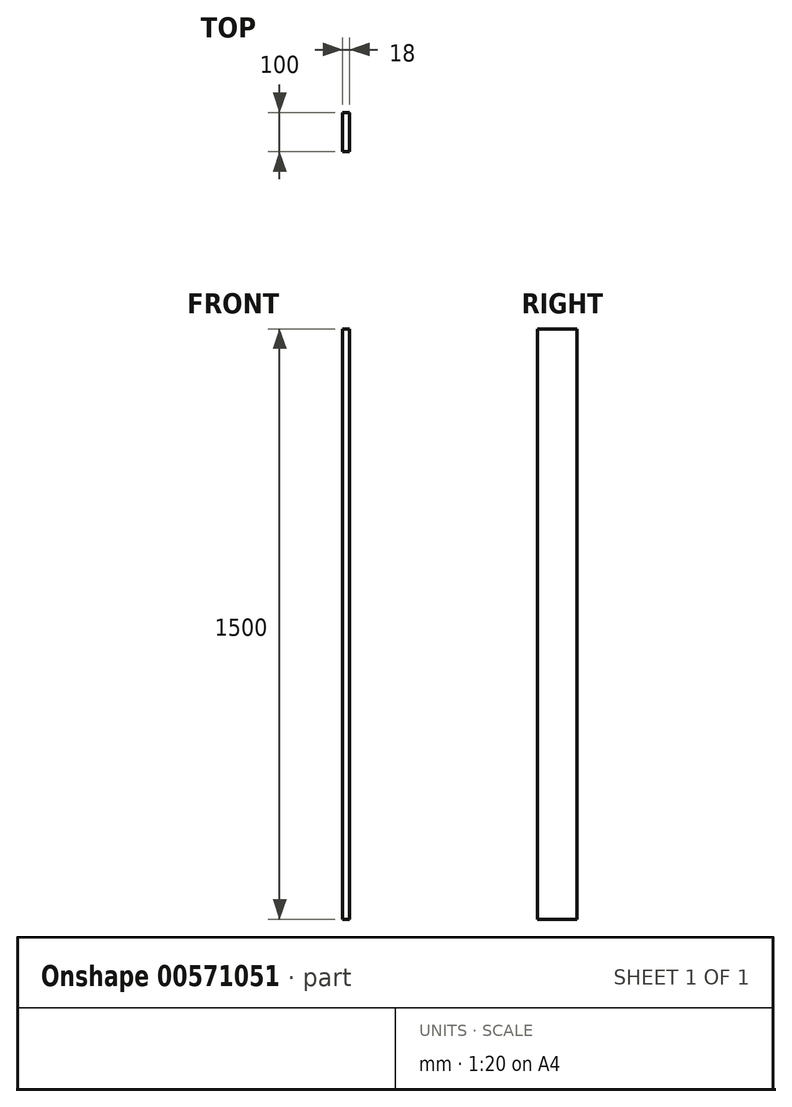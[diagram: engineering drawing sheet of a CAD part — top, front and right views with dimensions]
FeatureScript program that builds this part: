
annotation { "Feature Type Name" : "Feature", "Feature Type Description" : "" }
export const myFeature = defineFeature(function(context is Context, id is Id, definition is map)
    precondition{}
    {
        {
            var Q0;
            Q0=qCreatedBy(makeId("Right.planeOp"),FACE);
            var sketch = newSketch(context, id + "F0", { "sketchPlane" : qUnion([Q0])});
            skLineSegment(sketch, "E0.bottom", {"start": v(50, -750) * mm, "end": v(-50, -750) * mm});
            skLineSegment(sketch, "E0.top", {"start": v(50, 750) * mm, "end": v(-50, 750) * mm});
            skLineSegment(sketch, "E0.left", {"start": v(50, -750) * mm, "end": v(50, 750) * mm});
            skLineSegment(sketch, "E0.right", {"start": v(-50, -750) * mm, "end": v(-50, 750) * mm});
            skPoint(sketch, "E0.middle", {"position": v(0, 0) * mm});
            skSolve(sketch);
        }
        {
            var Q0;
            Q0 = qSketchRegion(id + "F0", true);
            extrude(context, id + "F1", {"entities" : qUnion([Q0]), "endBound" : BoundingType.SYMMETRIC, "depth" : 18 * mm, "offsetDistance" : 25 * mm});
        }
        {
            var Q0;
            Q0=makeQuery(id+"F1.opExtrude","SWEPT_BODY",BODY,{"disambiguationData":[OSD([sQuery(id+"F0.wireOp",EDGE,"E0.bottom"),sQuery(id+"F0.wireOp",EDGE,"E0.top"),sQuery(id+"F0.wireOp",EDGE,"E0.left"),sQuery(id+"F0.wireOp",EDGE,"E0.right")])]});
            var Q1;
            Q1=qCreatedBy(makeId("Origin.pointOp"),VERTEX);
            var Q2;
            Q2=qCreatedBy(makeId("Right.planeOp"),FACE);
            transform(context, id + "F2", {"entities" : qUnion([Q0]), "transformType" : TransformType.TRANSLATION_DISTANCE, "transformDirection" : qUnion([Q2]), "distance" : 500 * mm, "makeCopy" : false});
        }
    });
